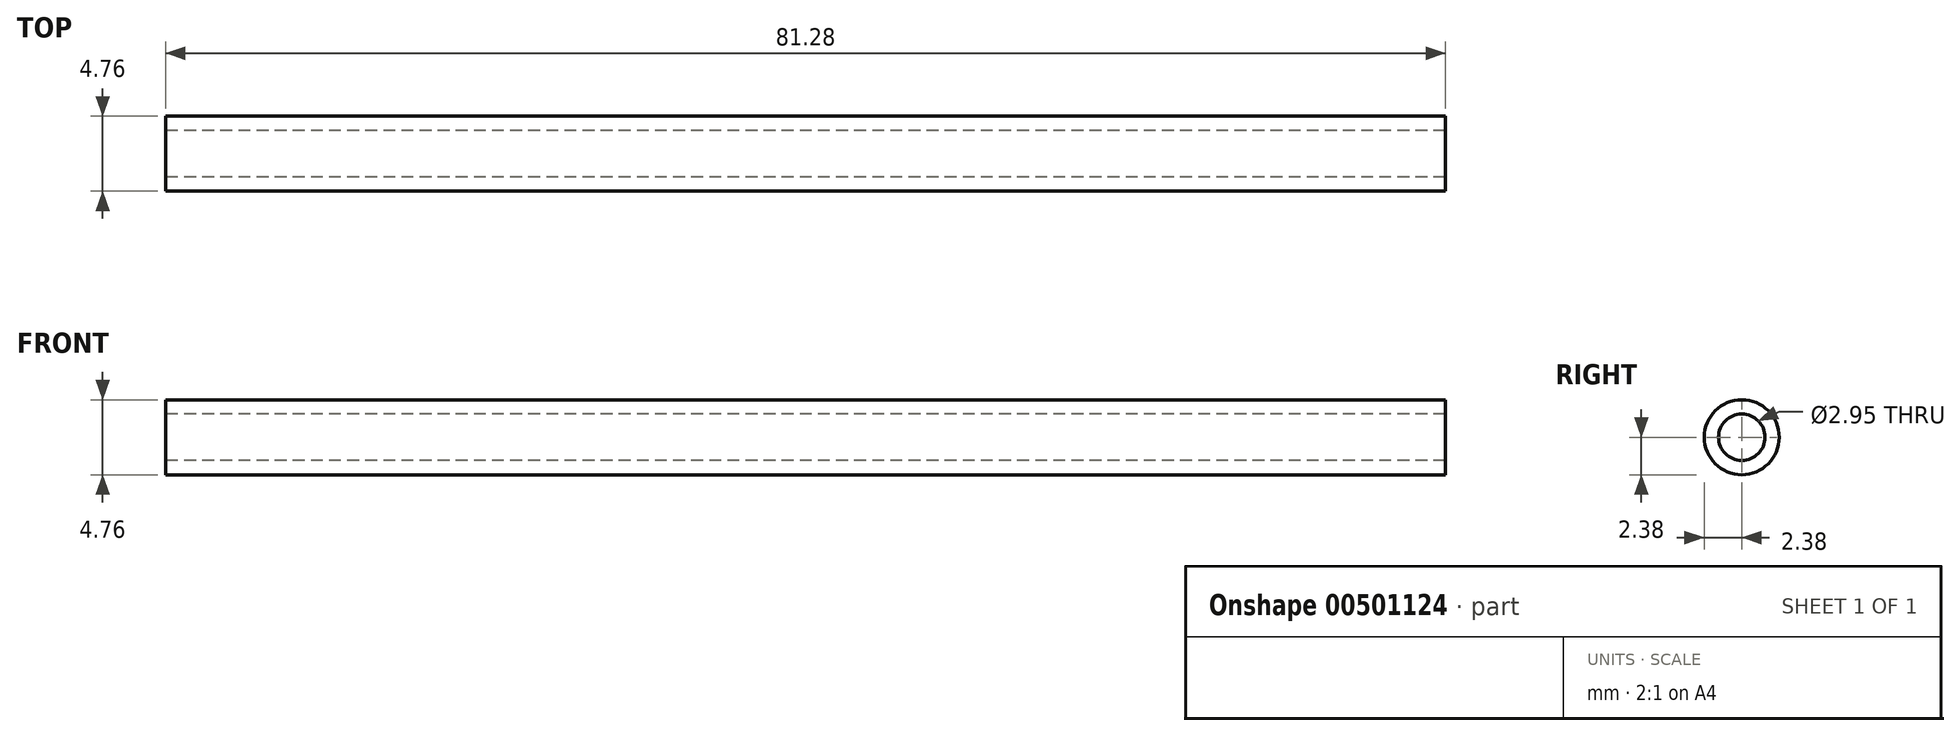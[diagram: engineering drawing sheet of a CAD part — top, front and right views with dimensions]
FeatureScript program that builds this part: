
annotation { "Feature Type Name" : "Feature", "Feature Type Description" : "" }
export const myFeature = defineFeature(function(context is Context, id is Id, definition is map)
    precondition{}
    {
        {
            var Q0;
            Q0=qCreatedBy(makeId("Right.planeOp"),FACE);
            var sketch = newSketch(context, id + "F0", { "sketchPlane" : qUnion([Q0])});
            skCircle(sketch, "E0", {"center": v(0, 0) * mm, "radius": 2.38 * mm});
            skCircle(sketch, "E1", {"center": v(0, 0) * mm, "radius": 1.47 * mm});
            skSolve(sketch);
        }
        {
            var Q0;
            Q0=qSketchRegion(id+"F0",true);
            extrude(context, id + "F1", {"entities" : qUnion([Q0]), "depth" : 81.28 * mm, "symmetric" : true});
        }
    });
